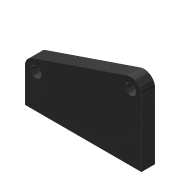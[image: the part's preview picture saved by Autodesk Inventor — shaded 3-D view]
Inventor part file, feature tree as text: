
AUTODESK INVENTOR PART (.ipt)
format: ipt  version: 2019.4 (Build 234330000, 330)  size: 89,600 bytes
history: native  units: mm
features: other x1, sketch x1, extrude x1, hole x1
ambient origin geometry x8: Origin, YZ Plane, XZ Plane, XY Plane, X Axis, Y Axis, Z Axis, Center Point
bodies: Body1 (feature_tree)
feature tree (4):
  other  "ソリッド1"
  sketch  "スケッチ1"
  extrude  "押し出し1"  Depth=35.0mm
  hole  "穴1"  [1 undecoded]
note: 1 required parameter value undecoded (feature->parameter linkage not recoverable at this tier; creation-order binding heuristic only, values carry confidence <= 0.55)
